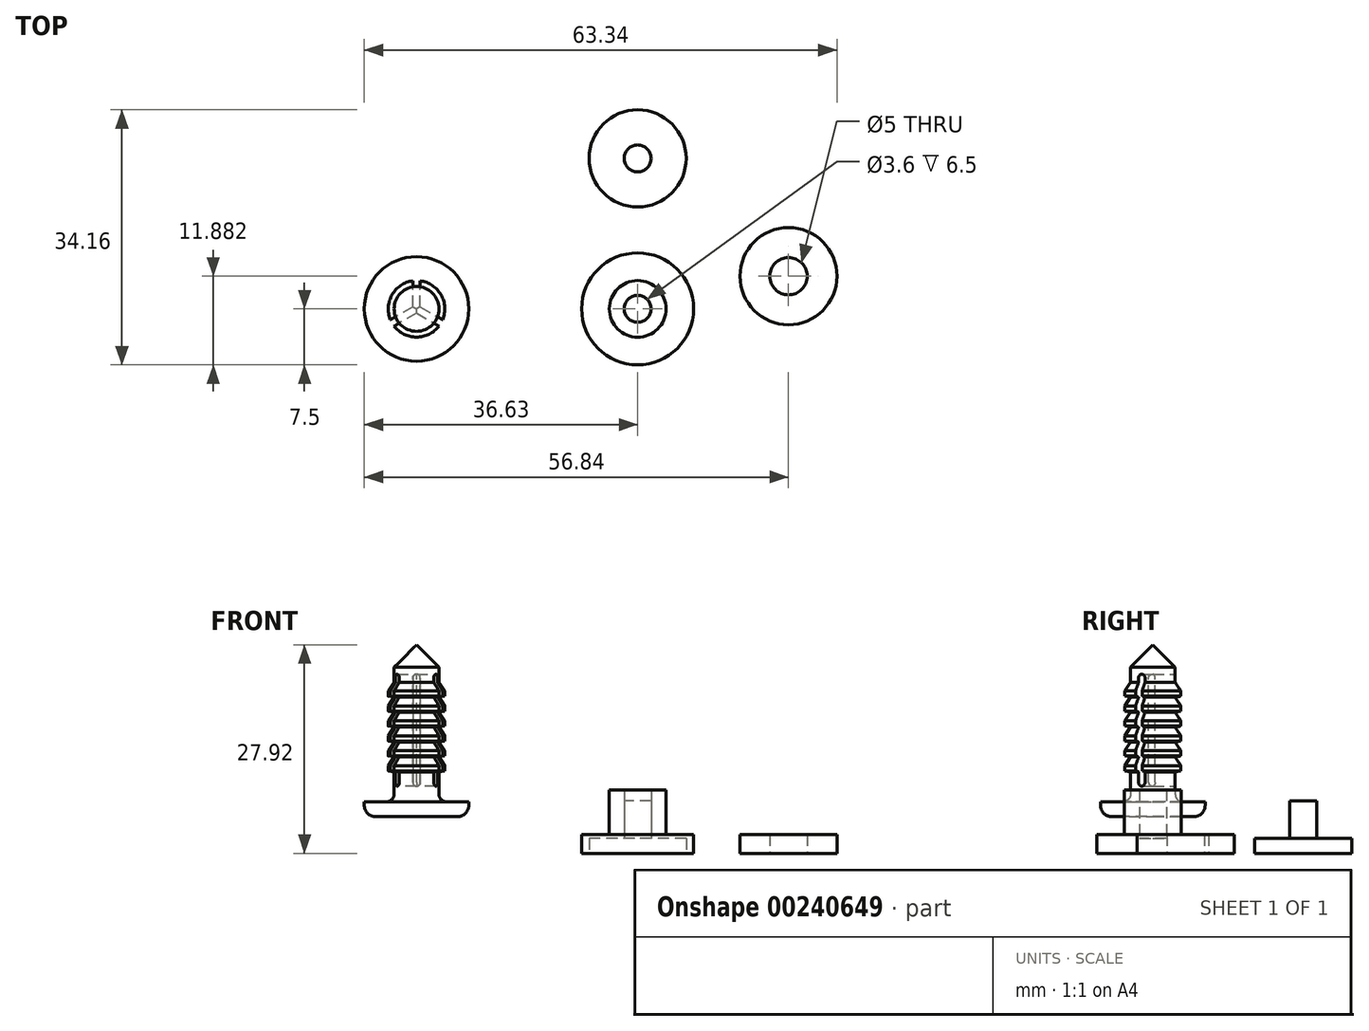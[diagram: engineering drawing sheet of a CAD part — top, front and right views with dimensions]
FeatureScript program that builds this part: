
annotation { "Feature Type Name" : "Feature", "Feature Type Description" : "" }
export const myFeature = defineFeature(function(context is Context, id is Id, definition is map)
    precondition{}
    {
        {
            var Q0;
            Q0=qCreatedBy(makeId("Top.planeOp"),FACE);
            var sketch = newSketch(context, id + "F0", { "sketchPlane" : qUnion([Q0])});
            skCircle(sketch, "E0", {"center": v(0, 0) * mm, "radius": 7.5 * mm});
            skSolve(sketch);
        }
        {
            var Q0;
            Q0=qSketchRegion(id+"F0",true);
            extrude(context, id + "F1", {"entities" : qUnion([Q0]), "depth" : 2.5 * mm});
        }
        {
            var Q0;
            Q0=makeQuery(id+"F1.opExtrude","CAP_FACE",FACE,{"disambiguationData":[OSD([sQuery(id+"F0.wireOp",EDGE,"E0")])],"isStart":false});
            var sketch = newSketch(context, id + "F2", { "sketchPlane" : qUnion([Q0])});
            skCircle(sketch, "E1", {"center": v(0, 0) * mm, "radius": 3.8 * mm});
            skSolve(sketch);
        }
        {
            var Q0;
            Q0=qSketchRegion(id+"F2",true);
            extrude(context, id + "F3", {"entities" : qUnion([Q0]), "operationType" : NewBodyOperationType.ADD, "depth" : 6 * mm});
        }
        {
            var Q0;
            Q0=makeQuery(id+"F3.opExtrude","CAP_FACE",FACE,{"disambiguationData":[OSD([sQuery(id+"F2.wireOp",EDGE,"E1")])],"isStart":false});
            shell(context, id + "F4", {"entities" : qUnion([Q0]), "thickness" : 2 * mm});
        }
        {
            var Q0;
            Q0=qCreatedBy(makeId("Top.planeOp"),FACE);
            var sketch = newSketch(context, id + "F5", { "sketchPlane" : qUnion([Q0])});
            skCircle(sketch, "E2", {"center": v(0, 20.16) * mm, "radius": 6.5 * mm});
            skSolve(sketch);
        }
        {
            var Q0;
            Q0=qSketchRegion(id+"F5",true);
            extrude(context, id + "F6", {"entities" : qUnion([Q0]), "depth" : 2 * mm});
        }
        {
            var Q0;
            Q0=makeQuery(id+"F6.opExtrude","CAP_FACE",FACE,{"disambiguationData":[OSD([sQuery(id+"F5.wireOp",EDGE,"E2")])],"isStart":false});
            var sketch = newSketch(context, id + "F7", { "sketchPlane" : qUnion([Q0])});
            skCircle(sketch, "E3", {"center": v(0, 20.16) * mm, "radius": 1.8 * mm});
            skSolve(sketch);
        }
        {
            var Q0;
            Q0=qSketchRegion(id+"F7",true);
            extrude(context, id + "F8", {"entities" : qUnion([Q0]), "operationType" : NewBodyOperationType.ADD, "depth" : 5 * mm});
        }
        {
            var Q0;
            Q0=qCreatedBy(makeId("Top.planeOp"),FACE);
            var sketch = newSketch(context, id + "F9", { "sketchPlane" : qUnion([Q0])});
            skCircle(sketch, "E4", {"center": v(20.2, 4.38) * mm, "radius": 6.5 * mm});
            skCircle(sketch, "E5", {"center": v(20.2, 4.38) * mm, "radius": 2.5 * mm});
            skSolve(sketch);
        }
        {
            var Q0;
            Q0=qSketchRegion(id+"F9",true);
            extrude(context, id + "F10", {"entities" : qUnion([Q0]), "depth" : 2.5 * mm});
        }
        {
            var Q0;
            Q0=qCreatedBy(makeId("Front.planeOp"),FACE);
            var sketch = newSketch(context, id + "F11", { "sketchPlane" : qUnion([Q0])});
            skLineSegment(sketch, "E6", {"start": v(-29.63, 4.92) * mm, "end": v(-36.63, 4.92) * mm});
            skLineSegment(sketch, "E7", {"start": v(-36.63, 4.92) * mm, "end": v(-36.63, 6.92) * mm});
            skLineSegment(sketch, "E8", {"start": v(-36.63, 6.92) * mm, "end": v(-32.63, 6.92) * mm});
            skLineSegment(sketch, "E9", {"start": v(-32.63, 6.92) * mm, "end": v(-32.63, 10.92) * mm});
            skLineSegment(sketch, "E10", {"start": v(-32.63, 10.92) * mm, "end": v(-33.42, 11.05) * mm});
            skLineSegment(sketch, "E11", {"start": v(-33.42, 11.05) * mm, "end": v(-33.42, 11.75) * mm});
            skLineSegment(sketch, "E12", {"start": v(-33.42, 11.75) * mm, "end": v(-32.63, 12.92) * mm});
            skLineSegment(sketch, "E13.1.0.0", {"start": v(-33.42, 13.75) * mm, "end": v(-32.63, 14.92) * mm});
            skLineSegment(sketch, "E13.1.0.1", {"start": v(-33.42, 13.05) * mm, "end": v(-33.42, 13.75) * mm});
            skLineSegment(sketch, "E13.1.0.2", {"start": v(-32.63, 12.92) * mm, "end": v(-33.42, 13.05) * mm});
            skLineSegment(sketch, "E13.2.0.0", {"start": v(-33.42, 15.75) * mm, "end": v(-32.63, 16.92) * mm});
            skLineSegment(sketch, "E13.2.0.1", {"start": v(-33.42, 15.05) * mm, "end": v(-33.42, 15.75) * mm});
            skLineSegment(sketch, "E13.2.0.2", {"start": v(-32.63, 14.92) * mm, "end": v(-33.42, 15.05) * mm});
            skLineSegment(sketch, "E13.3.0.0", {"start": v(-33.42, 17.75) * mm, "end": v(-32.63, 18.92) * mm});
            skLineSegment(sketch, "E13.3.0.1", {"start": v(-33.42, 17.05) * mm, "end": v(-33.42, 17.75) * mm});
            skLineSegment(sketch, "E13.3.0.2", {"start": v(-32.63, 16.92) * mm, "end": v(-33.42, 17.05) * mm});
            skLineSegment(sketch, "E13.4.0.0", {"start": v(-33.42, 19.75) * mm, "end": v(-32.63, 20.92) * mm});
            skLineSegment(sketch, "E13.4.0.1", {"start": v(-33.42, 19.05) * mm, "end": v(-33.42, 19.75) * mm});
            skLineSegment(sketch, "E13.4.0.2", {"start": v(-32.63, 18.92) * mm, "end": v(-33.42, 19.05) * mm});
            skLineSegment(sketch, "E13.direction1", {"start": v(-33.42, 11.75) * mm, "end": v(-33.42, 13.75) * mm, "construction": true});
            skLineSegment(sketch, "E14.0.5.0", {"start": v(-33.42, 21.75) * mm, "end": v(-32.63, 22.92) * mm});
            skLineSegment(sketch, "E14.3.5.0", {"start": v(-33.42, 21.05) * mm, "end": v(-33.42, 21.75) * mm});
            skLineSegment(sketch, "E14.6.5.0", {"start": v(-32.63, 20.92) * mm, "end": v(-33.42, 21.05) * mm});
            skLineSegment(sketch, "E15", {"start": v(-29.63, 4.92) * mm, "end": v(-29.63, 27.92) * mm});
            skLineSegment(sketch, "E16", {"start": v(-29.63, 27.92) * mm, "end": v(-32.63, 24.92) * mm});
            skLineSegment(sketch, "E17", {"start": v(-32.63, 22.92) * mm, "end": v(-32.63, 24.92) * mm});
            skSolve(sketch);
        }
        {
            var Q0;
            Q0 = qSketchRegion(id + "F11", true);
            var Q1;
            Q1=sQuery(id+"F11.wireOp",EDGE,"E15");
            revolve(context, id + "F12", {"entities" : qUnion([Q0]), "axis" : qUnion([Q1]), "revolveType" : RevolveType.FULL});
        }
        {
            var Q0;
            Q0=qCreatedBy(makeId("Top.planeOp"),FACE);
            cPlane(context, id + "F13", {"entities" : qUnion([Q0]), "cplaneType" : CPlaneType.OFFSET, "offset" : 24 * mm, "width" : 150 * mm, "height" : 150 * mm});
        }
        {
            var Q0;
            Q0=qCreatedBy(id+"F13.planeOp",FACE);
            var sketch = newSketch(context, id + "F14", { "sketchPlane" : qUnion([Q0])});
            skLineSegment(sketch, "E18.bottom", {"start": v(-30.13, 0) * mm, "end": v(-29.13, 0) * mm});
            skLineSegment(sketch, "E18.top", {"start": v(-30.13, 12) * mm, "end": v(-29.13, 12) * mm});
            skLineSegment(sketch, "E18.left", {"start": v(-30.13, 0) * mm, "end": v(-30.13, 12) * mm});
            skLineSegment(sketch, "E18.right", {"start": v(-29.13, 0) * mm, "end": v(-29.13, 12) * mm});
            skPoint(sketch, "E19", {"position": v(-29.63, 0) * mm});
            skLineSegment(sketch, "E20.1.1", {"start": v(-29.38, -0.43) * mm, "end": v(-39.77, -6.43) * mm});
            skLineSegment(sketch, "E20.1.2", {"start": v(-29.88, 0.43) * mm, "end": v(-40.27, -5.57) * mm});
            skLineSegment(sketch, "E20.1.3", {"start": v(-39.77, -6.43) * mm, "end": v(-40.27, -5.57) * mm});
            skLineSegment(sketch, "E20.1.4", {"start": v(-29.38, -0.43) * mm, "end": v(-29.88, 0.43) * mm});
            skLineSegment(sketch, "E20.2.1", {"start": v(-29.38, 0.43) * mm, "end": v(-18.99, -5.57) * mm});
            skLineSegment(sketch, "E20.2.2", {"start": v(-29.88, -0.43) * mm, "end": v(-19.49, -6.43) * mm});
            skLineSegment(sketch, "E20.2.3", {"start": v(-18.99, -5.57) * mm, "end": v(-19.49, -6.43) * mm});
            skLineSegment(sketch, "E20.2.4", {"start": v(-29.38, 0.43) * mm, "end": v(-29.88, -0.43) * mm});
            skSolve(sketch);
        }
        {
            var Q0;
            Q0 = qSketchRegion(id + "F14", true);
            extrude(context, id + "F15", {"entities" : qUnion([Q0]), "operationType" : NewBodyOperationType.REMOVE, "oppositeDirection" : true, "depth" : 15 * mm});
        }
        {
            var Q0;
            Q0=makeQuery(id+"F12.opRevolve","SWEPT_EDGE",EDGE,{"disambiguationData":[OSD([sQuery(id+"F11.wireOp",EDGE,"E8"),sQuery(id+"F11.wireOp",EDGE,"E9")])]});
            fillet(context, id + "F16", {"entities" : qUnion([Q0]), "radius" : 1 * mm, "tangentPropagation" : true, "allowEdgeOverflow" : false});
        }
        {
            var Q0;
            Q0=makeQuery(id+"F12.opRevolve","SWEPT_EDGE",EDGE,{"disambiguationData":[OSD([sQuery(id+"F11.wireOp",EDGE,"E6"),sQuery(id+"F11.wireOp",EDGE,"E7")])]});
            fillet(context, id + "F17", {"entities" : qUnion([Q0]), "radius" : 1.5 * mm, "tangentPropagation" : true, "allowEdgeOverflow" : false});
        }
        {
            var Q0;
            {var subQ0=sQuery(id+"F14.wireOp",EDGE,"E18.right");Q0=makeQuery(id+"F15.boolean.opBoolean","COPY",EDGE,{"derivedFrom":makeQuery(id+"F15.opExtrude","CAP_EDGE",EDGE,{"disambiguationData":[OSD([subQ0]),TDD([makeQuery(id+"F14.imprint","IMPRINT",EDGE,{"disambiguationData":[TD([[makeQuery(id+"F14.imprint","INTERSECT",VERTEX,{"derivedFrom":[subQ0,sQuery(id+"F14.wireOp",EDGE,"9WkbOore-7fF1-EQLA-wOVJ-1REbBUBYgNCd.top")]}),-1.0]])],"derivedFrom":subQ0}),makeQuery(id+"F14.imprint","IMPRINT",EDGE,{"disambiguationData":[TD([[makeQuery(id+"F14.imprint","INTERSECT",VERTEX,{"derivedFrom":[sQuery(id+"F14.wireOp",EDGE,"E18.top"),subQ0]}),1.0]])],"derivedFrom":subQ0})])],"isStart":false})});}
            var Q1;
            {var subQ0=sQuery(id+"F14.wireOp",EDGE,"E18.left");Q1=makeQuery(id+"F15.boolean.opBoolean","COPY",EDGE,{"derivedFrom":makeQuery(id+"F15.opExtrude","CAP_EDGE",EDGE,{"disambiguationData":[OSD([subQ0]),TDD([makeQuery(id+"F14.imprint","IMPRINT",EDGE,{"disambiguationData":[TD([[makeQuery(id+"F14.imprint","INTERSECT",VERTEX,{"derivedFrom":[subQ0,sQuery(id+"F14.wireOp",EDGE,"9WkbOore-7fF1-EQLA-wOVJ-1REbBUBYgNCd.top")]}),-1.0]])],"derivedFrom":subQ0}),makeQuery(id+"F14.imprint","IMPRINT",EDGE,{"disambiguationData":[TD([[makeQuery(id+"F14.imprint","INTERSECT",VERTEX,{"derivedFrom":[sQuery(id+"F14.wireOp",EDGE,"E18.top"),subQ0]}),1.0]])],"derivedFrom":subQ0})])],"isStart":false})});}
            var Q2;
            {var subQ0=sQuery(id+"F14.wireOp",EDGE,"9WkbOore-7fF1-EQLA-wOVJ-1REbBUBYgNCd.top");Q2=makeQuery(id+"F15.boolean.opBoolean","COPY",EDGE,{"derivedFrom":makeQuery(id+"F15.opExtrude","CAP_EDGE",EDGE,{"disambiguationData":[OSD([subQ0]),TDD([makeQuery(id+"F14.imprint","IMPRINT",EDGE,{"disambiguationData":[TD([[makeQuery(id+"F14.imprint","INTERSECT",VERTEX,{"derivedFrom":[subQ0,sQuery(id+"F14.wireOp",EDGE,"9WkbOore-7fF1-EQLA-wOVJ-1REbBUBYgNCd.left")]}),-1.0]])],"derivedFrom":subQ0}),makeQuery(id+"F14.imprint","IMPRINT",EDGE,{"disambiguationData":[TD([[makeQuery(id+"F14.imprint","INTERSECT",VERTEX,{"derivedFrom":[sQuery(id+"F14.wireOp",EDGE,"E18.left"),subQ0]}),1.0]])],"derivedFrom":subQ0})])],"isStart":false})});}
            var Q3;
            {var subQ0=sQuery(id+"F14.wireOp",EDGE,"9WkbOore-7fF1-EQLA-wOVJ-1REbBUBYgNCd.bottom");Q3=makeQuery(id+"F15.boolean.opBoolean","COPY",EDGE,{"derivedFrom":makeQuery(id+"F15.opExtrude","CAP_EDGE",EDGE,{"disambiguationData":[OSD([subQ0]),TDD([makeQuery(id+"F14.imprint","IMPRINT",EDGE,{"disambiguationData":[TD([[makeQuery(id+"F14.imprint","INTERSECT",VERTEX,{"derivedFrom":[subQ0,sQuery(id+"F14.wireOp",EDGE,"9WkbOore-7fF1-EQLA-wOVJ-1REbBUBYgNCd.left")]}),-1.0]])],"derivedFrom":subQ0}),makeQuery(id+"F14.imprint","IMPRINT",EDGE,{"disambiguationData":[TD([[makeQuery(id+"F14.imprint","INTERSECT",VERTEX,{"derivedFrom":[sQuery(id+"F14.wireOp",EDGE,"E18.left"),subQ0]}),1.0]])],"derivedFrom":subQ0})])],"isStart":false})});}
            var Q4;
            {var subQ0=sQuery(id+"F14.wireOp",EDGE,"E18.left");Q4=makeQuery(id+"F15.boolean.opBoolean","COPY",EDGE,{"derivedFrom":makeQuery(id+"F15.opExtrude","CAP_EDGE",EDGE,{"disambiguationData":[OSD([subQ0]),TDD([makeQuery(id+"F14.imprint","IMPRINT",EDGE,{"disambiguationData":[TD([[makeQuery(id+"F14.imprint","INTERSECT",VERTEX,{"derivedFrom":[sQuery(id+"F14.wireOp",EDGE,"E18.bottom"),subQ0]}),-1.0]])],"derivedFrom":subQ0}),makeQuery(id+"F14.imprint","IMPRINT",EDGE,{"disambiguationData":[TD([[makeQuery(id+"F14.imprint","INTERSECT",VERTEX,{"derivedFrom":[subQ0,sQuery(id+"F14.wireOp",EDGE,"9WkbOore-7fF1-EQLA-wOVJ-1REbBUBYgNCd.bottom")]}),1.0]])],"derivedFrom":subQ0})])],"isStart":false})});}
            var Q5;
            {var subQ0=sQuery(id+"F14.wireOp",EDGE,"E18.right");Q5=makeQuery(id+"F15.boolean.opBoolean","COPY",EDGE,{"derivedFrom":makeQuery(id+"F15.opExtrude","CAP_EDGE",EDGE,{"disambiguationData":[OSD([subQ0]),TDD([makeQuery(id+"F14.imprint","IMPRINT",EDGE,{"disambiguationData":[TD([[makeQuery(id+"F14.imprint","INTERSECT",VERTEX,{"derivedFrom":[sQuery(id+"F14.wireOp",EDGE,"E18.bottom"),subQ0]}),-1.0]])],"derivedFrom":subQ0}),makeQuery(id+"F14.imprint","IMPRINT",EDGE,{"disambiguationData":[TD([[makeQuery(id+"F14.imprint","INTERSECT",VERTEX,{"derivedFrom":[subQ0,sQuery(id+"F14.wireOp",EDGE,"9WkbOore-7fF1-EQLA-wOVJ-1REbBUBYgNCd.bottom")]}),1.0]])],"derivedFrom":subQ0})])],"isStart":false})});}
            var Q6;
            {var subQ0=sQuery(id+"F14.wireOp",EDGE,"9WkbOore-7fF1-EQLA-wOVJ-1REbBUBYgNCd.bottom");Q6=makeQuery(id+"F15.boolean.opBoolean","COPY",EDGE,{"derivedFrom":makeQuery(id+"F15.opExtrude","CAP_EDGE",EDGE,{"disambiguationData":[OSD([subQ0]),TDD([makeQuery(id+"F14.imprint","IMPRINT",EDGE,{"disambiguationData":[TD([[makeQuery(id+"F14.imprint","INTERSECT",VERTEX,{"derivedFrom":[sQuery(id+"F14.wireOp",EDGE,"E18.right"),subQ0]}),-1.0]])],"derivedFrom":subQ0}),makeQuery(id+"F14.imprint","IMPRINT",EDGE,{"disambiguationData":[TD([[makeQuery(id+"F14.imprint","INTERSECT",VERTEX,{"derivedFrom":[subQ0,sQuery(id+"F14.wireOp",EDGE,"9WkbOore-7fF1-EQLA-wOVJ-1REbBUBYgNCd.right")]}),1.0]])],"derivedFrom":subQ0})])],"isStart":false})});}
            var Q7;
            {var subQ0=sQuery(id+"F14.wireOp",EDGE,"9WkbOore-7fF1-EQLA-wOVJ-1REbBUBYgNCd.top");Q7=makeQuery(id+"F15.boolean.opBoolean","COPY",EDGE,{"derivedFrom":makeQuery(id+"F15.opExtrude","CAP_EDGE",EDGE,{"disambiguationData":[OSD([subQ0]),TDD([makeQuery(id+"F14.imprint","IMPRINT",EDGE,{"disambiguationData":[TD([[makeQuery(id+"F14.imprint","INTERSECT",VERTEX,{"derivedFrom":[sQuery(id+"F14.wireOp",EDGE,"E18.right"),subQ0]}),-1.0]])],"derivedFrom":subQ0}),makeQuery(id+"F14.imprint","IMPRINT",EDGE,{"disambiguationData":[TD([[makeQuery(id+"F14.imprint","INTERSECT",VERTEX,{"derivedFrom":[subQ0,sQuery(id+"F14.wireOp",EDGE,"9WkbOore-7fF1-EQLA-wOVJ-1REbBUBYgNCd.right")]}),1.0]])],"derivedFrom":subQ0})])],"isStart":false})});}
            var Q8;
            Q8=makeQuery(id+"F15.boolean.opBoolean","COPY",EDGE,{"derivedFrom":makeQuery(id+"F15.opExtrude","CAP_EDGE",EDGE,{"disambiguationData":[OSD([sQuery(id+"F14.wireOp",EDGE,"E20.2.1")])],"isStart":false})});
            var Q9;
            Q9=makeQuery(id+"F15.boolean.opBoolean","COPY",EDGE,{"derivedFrom":makeQuery(id+"F15.opExtrude","CAP_EDGE",EDGE,{"disambiguationData":[OSD([sQuery(id+"F14.wireOp",EDGE,"E20.2.2")])],"isStart":false})});
            var Q10;
            Q10=makeQuery(id+"F15.boolean.opBoolean","COPY",EDGE,{"derivedFrom":makeQuery(id+"F15.opExtrude","CAP_EDGE",EDGE,{"disambiguationData":[OSD([sQuery(id+"F14.wireOp",EDGE,"E20.1.2")])],"isStart":false})});
            var Q11;
            Q11=makeQuery(id+"F15.boolean.opBoolean","COPY",EDGE,{"derivedFrom":makeQuery(id+"F15.opExtrude","CAP_EDGE",EDGE,{"disambiguationData":[OSD([sQuery(id+"F14.wireOp",EDGE,"E20.1.1")])],"isStart":false})});
            var Q12;
            Q12=makeQuery(id+"F15.boolean.opBoolean","COPY",EDGE,{"derivedFrom":makeQuery(id+"F15.opExtrude","CAP_EDGE",EDGE,{"disambiguationData":[OSD([sQuery(id+"F14.wireOp",EDGE,"E18.right")])],"isStart":true})});
            var Q13;
            Q13=makeQuery(id+"F15.boolean.opBoolean","COPY",EDGE,{"derivedFrom":makeQuery(id+"F15.opExtrude","CAP_EDGE",EDGE,{"disambiguationData":[OSD([sQuery(id+"F14.wireOp",EDGE,"E20.1.2")])],"isStart":true})});
            var Q14;
            Q14=makeQuery(id+"F15.boolean.opBoolean","COPY",EDGE,{"derivedFrom":makeQuery(id+"F15.opExtrude","CAP_EDGE",EDGE,{"disambiguationData":[OSD([sQuery(id+"F14.wireOp",EDGE,"E20.2.1")])],"isStart":true})});
            var Q15;
            Q15=makeQuery(id+"F15.boolean.opBoolean","COPY",EDGE,{"derivedFrom":makeQuery(id+"F15.opExtrude","CAP_EDGE",EDGE,{"disambiguationData":[OSD([sQuery(id+"F14.wireOp",EDGE,"E20.1.1")])],"isStart":true})});
            var Q16;
            Q16=makeQuery(id+"F15.boolean.opBoolean","COPY",EDGE,{"derivedFrom":makeQuery(id+"F15.opExtrude","CAP_EDGE",EDGE,{"disambiguationData":[OSD([sQuery(id+"F14.wireOp",EDGE,"E18.left")])],"isStart":true})});
            var Q17;
            Q17=makeQuery(id+"F15.boolean.opBoolean","COPY",EDGE,{"derivedFrom":makeQuery(id+"F15.opExtrude","CAP_EDGE",EDGE,{"disambiguationData":[OSD([sQuery(id+"F14.wireOp",EDGE,"E20.2.2")])],"isStart":true})});
            fillet(context, id + "F18", {"entities" : qUnion([Q0, Q1, Q2, Q3, Q4, Q5, Q6, Q7, Q8, Q9, Q10, Q11, Q12, Q13, Q14, Q15, Q16, Q17]), "radius" : 0.5 * mm, "tangentPropagation" : true, "allowEdgeOverflow" : false});
        }
    });
